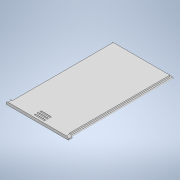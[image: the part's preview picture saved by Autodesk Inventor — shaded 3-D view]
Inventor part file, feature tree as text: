
AUTODESK INVENTOR PART (.ipt)
format: ipt  version: 2020.2 (Build 242310000, 310)  size: 185,856 bytes
history: native  units: mm
features: extrude x5, sketch x5, fillet x1
ambient origin geometry x8: Origin, YZ Plane, XZ Plane, XY Plane, X Axis, Y Axis, Z Axis, Center Point
bodies: Solid1 (feature_tree)
feature tree (11):
  extrude  "Extrusion1"  Depth=3.0mm
  extrude  "Extrusion2"  Depth=4.0mm
  fillet  "Fillet1"  Radius=0.0mm
  extrude  "Extrusion3"  TaperAngle=90.0deg  [1 undecoded]
  extrude  "Extrusion4"  Depth=1.5mm
  extrude  "Extrusion5"  Depth=2.0mm
  sketch  "Sketch1"  dims[d0=67.0mm d1=3.0mm]
  sketch  "Sketch3"  dims[d2=4.0mm d3=0.0mm d16=33.5mm d17=0.0mm]
  sketch  "Sketch5"  dims[d18=0.75mm d19=90.0deg]
  sketch  "Sketch6"  dims[d20=32.0mm d21=1.5mm]
  sketch  "Sketch7"  dims[d22=113.75mm d23=0.0mm d24=2.0mm d29=3.0mm d30=61.0mm d31=180.0deg d32=3.0mm d33=180.0deg d34=61.0mm d35=108.4mm d36=1.5mm d37=0.0mm d38=33.5mm d39=2.0mm d40=20.0mm d41=1.25mm d42=1.0mm d43=-12.217305mm d44=33.5mm d45=3.0mm d46=5.0mm d47=180.0deg d48=1.5mm d49=3.0mm d50=90.0deg d51=5.0mm d52=180.0deg d53=1.5mm d54=3.0mm d55=90.0deg d56=5.0mm d57=1.5mm d58=1.5mm d59=-9.599311mm]
note: 1 required parameter value undecoded (feature->parameter linkage not recoverable at this tier; creation-order binding heuristic only, values carry confidence <= 0.55)
